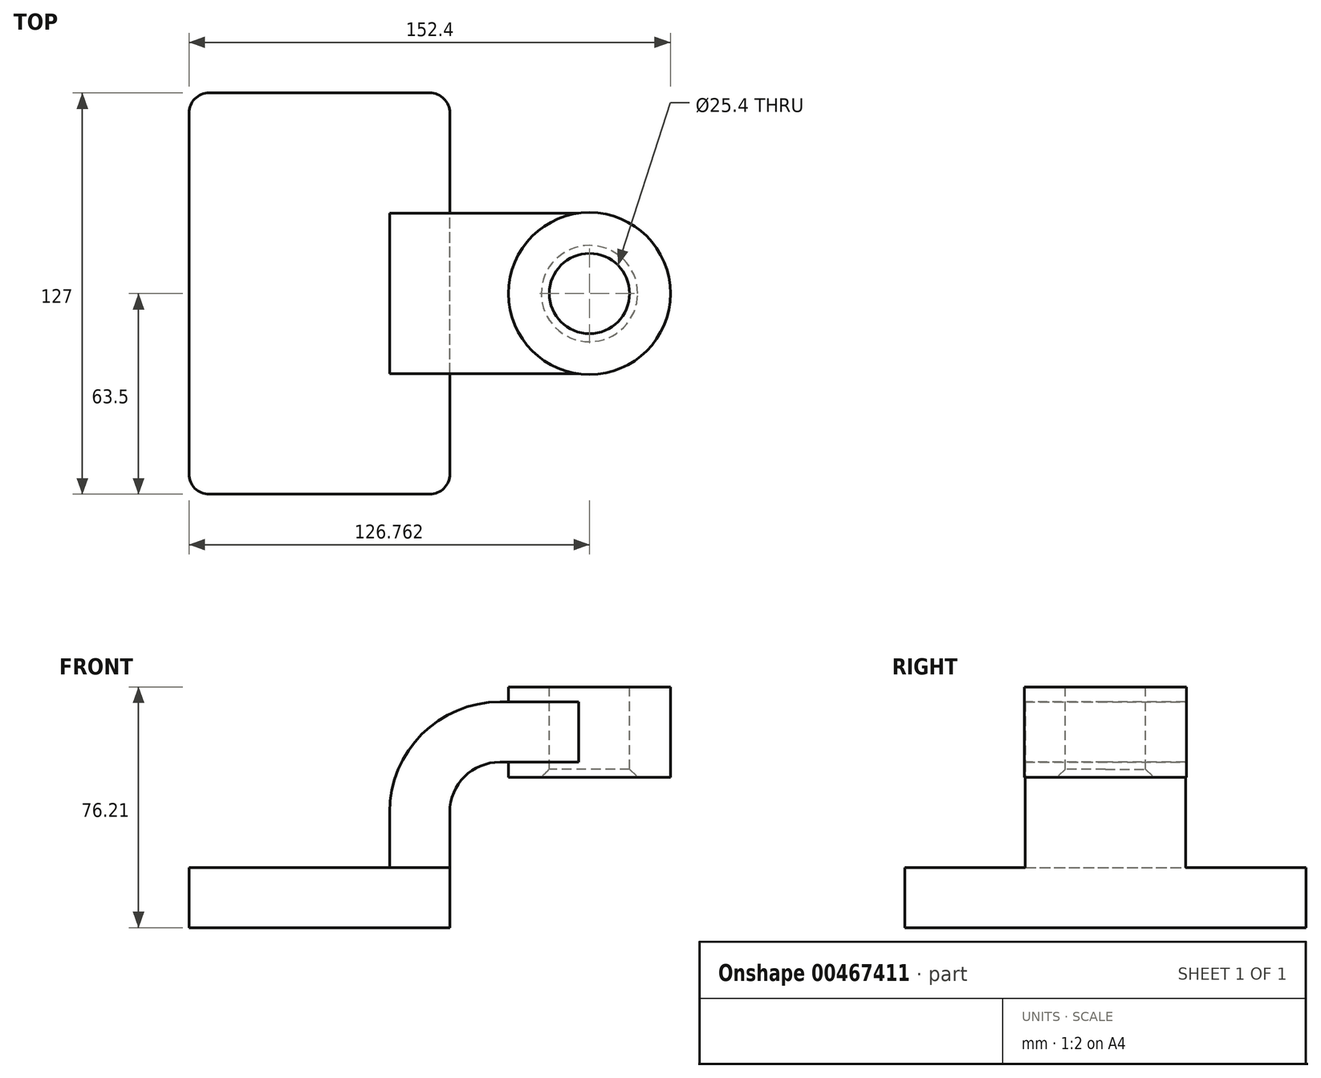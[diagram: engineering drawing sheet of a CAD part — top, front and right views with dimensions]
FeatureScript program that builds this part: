
annotation { "Feature Type Name" : "Feature", "Feature Type Description" : "" }
export const myFeature = defineFeature(function(context is Context, id is Id, definition is map)
    precondition{}
    {
        {
            var Q0;
            Q0=qCreatedBy(makeId("Front.planeOp"),FACE);
            var sketch = newSketch(context, id + "F0", { "sketchPlane" : qUnion([Q0])});
            skLineSegment(sketch, "E0.bottom", {"start": v(-41.28, -9.53) * mm, "end": v(41.28, -9.53) * mm});
            skLineSegment(sketch, "E0.top", {"start": v(-41.28, 9.53) * mm, "end": v(41.28, 9.53) * mm});
            skLineSegment(sketch, "E0.left", {"start": v(-41.28, -9.53) * mm, "end": v(-41.28, 9.53) * mm});
            skLineSegment(sketch, "E0.right", {"start": v(41.28, -9.53) * mm, "end": v(41.28, 9.53) * mm});
            skPoint(sketch, "E0.middle", {"position": v(0, 0) * mm});
            skLineSegment(sketch, "E1.bottom", {"start": v(60.32, 38.1) * mm, "end": v(111.12, 38.1) * mm});
            skLineSegment(sketch, "E1.top", {"start": v(60.32, 66.67) * mm, "end": v(111.12, 66.67) * mm});
            skLineSegment(sketch, "E1.left", {"start": v(60.32, 38.1) * mm, "end": v(60.32, 42.88) * mm});
            skLineSegment(sketch, "E1.right", {"start": v(111.12, 38.1) * mm, "end": v(111.12, 66.67) * mm});
            skPoint(sketch, "E1.middle", {"position": v(85.72, 52.39) * mm});
            skLineSegment(sketch, "E2", {"start": v(41.28, 9.52) * mm, "end": v(41.28, 27) * mm});
            skArc(sketch, "E3", {"start": v(41.27, 27) * mm, "mid": v(45.92, 38.23) * mm, "end": v(57.15, 42.88) * mm});
            skLineSegment(sketch, "E4", {"start": v(57.15, 42.88) * mm, "end": v(85.5, 42.88) * mm});
            skLineSegment(sketch, "E5.0", {"start": v(57.15, 61.93) * mm, "end": v(85.5, 61.93) * mm});
            skArc(sketch, "E5.1", {"start": v(22.22, 27) * mm, "mid": v(32.45, 51.7) * mm, "end": v(57.15, 61.93) * mm});
            skLineSegment(sketch, "E5.2", {"start": v(22.22, 9.52) * mm, "end": v(22.22, 27) * mm});
            skLineSegment(sketch, "E6", {"start": v(85.5, 42.88) * mm, "end": v(85.5, 61.93) * mm});
            skFitSpline(sketch, "E7", {"points": [v(-41.28, 9.53) * mm, v(57.15, 61.93) * mm], "startDerivative": vector(1.55, 103.25) * mm, "endDerivative": vector(115.52, -0.01) * mm});
            skLineSegment(sketch, "E8", {"start": v(85.5, 42.88) * mm, "end": v(85.5, 38.1) * mm});
            skLineSegment(sketch, "E9", {"start": v(85.5, 61.93) * mm, "end": v(85.5, 66.67) * mm});
            skLineSegment(sketch, "E10.trimOffspring", {"start": v(60.32, 61.93) * mm, "end": v(60.32, 66.67) * mm});
            skSolve(sketch);
        }
        {
            var Q0;
            Q0=makeQuery(id+"F0.imprint","IMPRINT",FACE,{"disambiguationData":[TD([[makeQuery(id+"F0.imprint","IMPRINT",EDGE,{"derivedFrom":sQuery(id+"F0.wireOp",EDGE,"E0.bottom")}),1.0]])]});
            extrude(context, id + "F1", {"entities" : qUnion([Q0]), "endBound" : BoundingType.SYMMETRIC, "depth" : 127 * mm});
        }
        {
            var Q0;
            {var subQ0=sQuery(id+"F0.wireOp",EDGE,"E2");Q0=makeQuery(id+"F0.imprint","IMPRINT",FACE,{"disambiguationData":[TD([[makeQuery(id+"F0.imprint","IMPRINT",EDGE,{"derivedFrom":subQ0}),1.0]])]});}
            extrude(context, id + "F2", {"entities" : qUnion([Q0]), "operationType" : NewBodyOperationType.ADD, "endBound" : BoundingType.SYMMETRIC, "depth" : 50.8 * mm});
        }
        {
            var Q0;
            Q0=makeQuery(id+"F0.imprint","IMPRINT",FACE,{"disambiguationData":[TD([[makeQuery(id+"F0.imprint","IMPRINT",EDGE,{"derivedFrom":sQuery(id+"F0.wireOp",EDGE,"E5.1")}),1.0]])]});
            extrude(context, id + "F3", {"entities" : qUnion([Q0]), "operationType" : NewBodyOperationType.ADD, "endBound" : BoundingType.SYMMETRIC, "depth" : 15.88 * mm});
        }
        {
            var Q0;
            {var subQ0=sQuery(id+"F0.wireOp",EDGE,"E1.right");Q0=makeQuery(id+"F0.imprint","IMPRINT",FACE,{"disambiguationData":[TD([[makeQuery(id+"F0.imprint","IMPRINT",EDGE,{"derivedFrom":subQ0}),1.0]])]});}
            var Q1;
            Q1=sQuery(id+"F0.wireOp",EDGE,"E6");
            revolve(context, id + "F4", {"operationType" : NewBodyOperationType.ADD, "entities" : qUnion([Q0]), "axis" : qUnion([Q1]), "revolveType" : RevolveType.FULL});
        }
        {
            var Q0;
            Q0=makeQuery(id+"F1.opExtrude","CAP_EDGE",EDGE,{"disambiguationData":[OSD([sQuery(id+"F0.wireOp",EDGE,"E0.left")])],"isStart":false});
            var Q1;
            Q1=makeQuery(id+"F1.opExtrude","CAP_EDGE",EDGE,{"disambiguationData":[OSD([sQuery(id+"F0.wireOp",EDGE,"E0.right")])],"isStart":false});
            var Q2;
            Q2=makeQuery(id+"F1.opExtrude","CAP_EDGE",EDGE,{"disambiguationData":[OSD([sQuery(id+"F0.wireOp",EDGE,"E0.right")])],"isStart":true});
            var Q3;
            Q3=makeQuery(id+"F1.opExtrude","CAP_EDGE",EDGE,{"disambiguationData":[OSD([sQuery(id+"F0.wireOp",EDGE,"E0.left")])],"isStart":true});
            fillet(context, id + "F5", {"entities" : qUnion([Q0, Q1, Q2, Q3]), "radius" : 6.35 * mm, "tangentPropagation" : true, "allowEdgeOverflow" : false});
        }
        {
            var Q0;
            Q0=makeQuery(id+"F4.opRevolve","SWEPT_FACE",FACE,{"disambiguationData":[OSD([sQuery(id+"F0.wireOp",EDGE,"E1.top")])]});
            var sketch = newSketch(context, id + "F6", { "sketchPlane" : qUnion([Q0])});
            skCircle(sketch, "E11", {"center": v(85.5, 0) * mm, "radius": 12.7 * mm});
            skSolve(sketch);
        }
        {
            var Q0;
            Q0=makeQuery(id+"F6.imprint","IMPRINT",FACE,{"disambiguationData":[TD([[makeQuery(id+"F6.imprint","IMPRINT",EDGE,{"derivedFrom":sQuery(id+"F6.wireOp",EDGE,"E11")}),1.0]])]});
            extrude(context, id + "F7", {"entities" : qUnion([Q0]), "operationType" : NewBodyOperationType.REMOVE, "endBound" : BoundingType.THROUGH_ALL, "oppositeDirection" : true, "depth" : 25.4 * mm});
        }
        {
            var Q0;
            Q0=makeQuery(id+"F7.boolean.opBoolean","COPY",EDGE,{"derivedFrom":makeQuery(id+"F7.opExtrude","CAP_EDGE",EDGE,{"disambiguationData":[OSD([sQuery(id+"F6.wireOp",EDGE,"E11")])],"isStart":true})});
            var Q1;
            Q1=makeQuery(id+"F7.boolean.opBoolean","INTERSECT",EDGE,{"derivedFrom":[makeQuery(id+"F4.opRevolve","SWEPT_FACE",FACE,{"disambiguationData":[OSD([sQuery(id+"F0.wireOp",EDGE,"E1.bottom")])]}),makeQuery(id+"F7.opExtrude","SWEPT_FACE",FACE,{"disambiguationData":[OSD([sQuery(id+"F6.wireOp",EDGE,"E11")])]})]});
            chamfer(context, id + "F8", {"entities" : qUnion([Q0, Q1]), "width" : 2.54 * mm, "tangentPropagation" : true});
        }
    });
